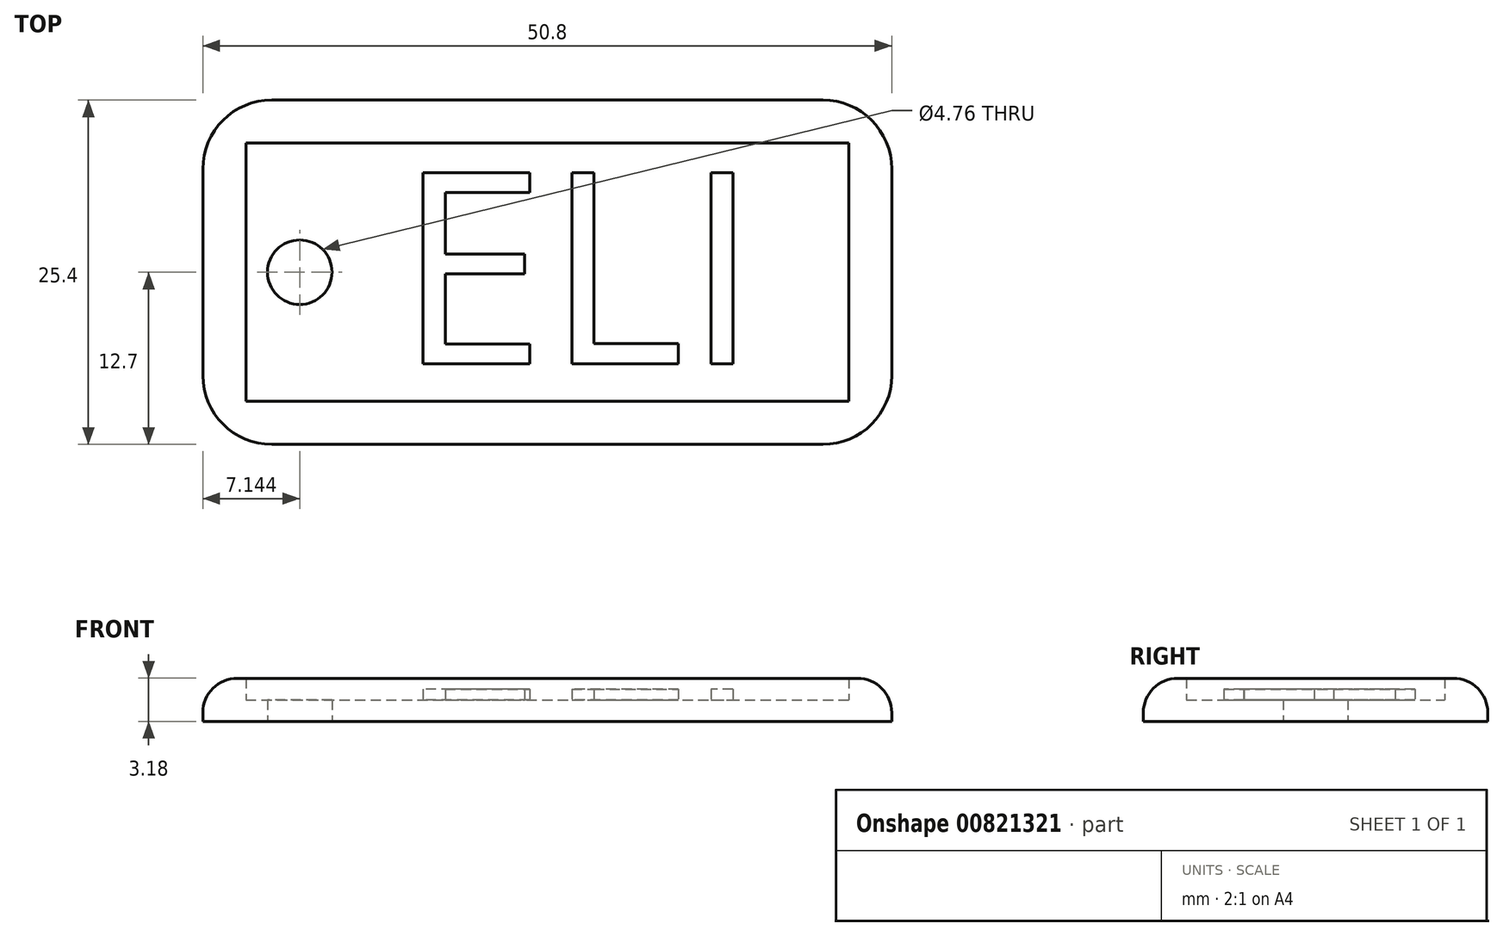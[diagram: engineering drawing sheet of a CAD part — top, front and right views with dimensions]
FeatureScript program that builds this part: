
annotation { "Feature Type Name" : "Feature", "Feature Type Description" : "" }
export const myFeature = defineFeature(function(context is Context, id is Id, definition is map)
    precondition{}
    {
        {
            var Q0;
            Q0=qCreatedBy(makeId("Top.planeOp"),FACE);
            var sketch = newSketch(context, id + "F0", { "sketchPlane" : qUnion([Q0])});
            skLineSegment(sketch, "E0.bottom", {"start": v(0, 0) * mm, "end": v(50.8, 0) * mm});
            skLineSegment(sketch, "E0.top", {"start": v(0, 25.4) * mm, "end": v(50.8, 25.4) * mm});
            skLineSegment(sketch, "E0.left", {"start": v(0, 0) * mm, "end": v(0, 25.4) * mm});
            skLineSegment(sketch, "E0.right", {"start": v(50.8, 0) * mm, "end": v(50.8, 25.4) * mm});
            skCircle(sketch, "E1", {"center": v(7.14, 12.7) * mm, "radius": 2.38 * mm});
            skPoint(sketch, "E1.centerSnap0", {"position": v(0, 12.7) * mm});
            skLineSegment(sketch, "E2.0", {"start": v(3.18, 22.23) * mm, "end": v(47.62, 22.23) * mm});
            skLineSegment(sketch, "E2.1", {"start": v(3.18, 3.18) * mm, "end": v(3.18, 22.22) * mm});
            skLineSegment(sketch, "E2.2", {"start": v(3.18, 3.18) * mm, "end": v(47.62, 3.18) * mm});
            skLineSegment(sketch, "E2.3", {"start": v(47.62, 3.18) * mm, "end": v(47.62, 22.23) * mm});
            skSolve(sketch);
        }
        {
            var Q0;
            Q0=makeQuery(id+"F0.imprint","IMPRINT",FACE,{"disambiguationData":[TD([[makeQuery(id+"F0.imprint","IMPRINT",EDGE,{"derivedFrom":sQuery(id+"F0.wireOp",EDGE,"E1")}),-1.0]])]});
            extrude(context, id + "F1", {"entities" : qUnion([Q0]), "depth" : 1.59 * mm, "offsetDistance" : 25.4 * mm});
        }
        {
            var Q0;
            Q0 = qSketchRegion(id + "F0", true);
            extrude(context, id + "F2", {"entities" : qUnion([Q0]), "operationType" : NewBodyOperationType.ADD, "depth" : 3.17 * mm, "offsetDistance" : 25.4 * mm});
        }
        {
            var Q0;
            Q0=makeQuery(id+"F2.opExtrude","SWEPT_EDGE",EDGE,{"disambiguationData":[OSD([sQuery(id+"F0.wireOp",EDGE,"E0.bottom"),sQuery(id+"F0.wireOp",EDGE,"E0.left")])]});
            var Q1;
            Q1=makeQuery(id+"F2.opExtrude","SWEPT_EDGE",EDGE,{"disambiguationData":[OSD([sQuery(id+"F0.wireOp",EDGE,"E0.bottom"),sQuery(id+"F0.wireOp",EDGE,"E0.right")])]});
            var Q2;
            Q2=makeQuery(id+"F2.opExtrude","SWEPT_EDGE",EDGE,{"disambiguationData":[OSD([sQuery(id+"F0.wireOp",EDGE,"E0.top"),sQuery(id+"F0.wireOp",EDGE,"E0.right")])]});
            var Q3;
            Q3=makeQuery(id+"F2.opExtrude","SWEPT_EDGE",EDGE,{"disambiguationData":[OSD([sQuery(id+"F0.wireOp",EDGE,"E0.top"),sQuery(id+"F0.wireOp",EDGE,"E0.left")])]});
            fillet(context, id + "F3", {"entities" : qUnion([Q0, Q1, Q2, Q3]), "radius" : 5.08 * mm, "tangentPropagation" : true, "allowEdgeOverflow" : false});
        }
        {
            var Q0;
            Q0=makeQuery(id+"F2.opExtrude","CAP_EDGE",EDGE,{"disambiguationData":[OSD([sQuery(id+"F0.wireOp",EDGE,"E0.bottom")])],"isStart":false});
            fillet(context, id + "F4", {"entities" : qUnion([Q0]), "radius" : 2.54 * mm, "tangentPropagation" : true, "allowEdgeOverflow" : false});
        }
        {
            var Q0;
            Q0=makeQuery(id+"F1.opExtrude","CAP_FACE",FACE,{"disambiguationData":[OSD([sQuery(id+"F0.wireOp",EDGE,"E1"),sQuery(id+"F0.wireOp",EDGE,"E2.0"),sQuery(id+"F0.wireOp",EDGE,"E2.1"),sQuery(id+"F0.wireOp",EDGE,"E2.2"),sQuery(id+"F0.wireOp",EDGE,"E2.3")])],"isStart":false});
            var sketch = newSketch(context, id + "F5", { "sketchPlane" : qUnion([Q0])});
            skText(sketch, "E3", { "text": "ELI", "fontName": "OpenSans-Regular.ttf"});
            const initialGuessF5  = {"E3": [0.0143, 0.00594, 1, 0, 0.01421]};
            skSetInitialGuess(sketch, initialGuessF5);
            skSolve(sketch);
        }
        {
            var Q0;
            Q0 = qSketchRegion(id + "F5", true);
            extrude(context, id + "F6", {"entities" : qUnion([Q0]), "operationType" : NewBodyOperationType.ADD, "depth" : 0.8 * mm, "offsetDistance" : 25.4 * mm});
        }
    });
